# Revit family: A1-160-B
name_source: partatom
category: Structural Connections
revit_build: Autodesk Revit 2015 (Build: 20140606_1530(x64)
units: mm (PartAtom-declared; Revit-internal decimal feet)

## types (1)
- A1-160-B
    Default Elevation = 0 mm  [stored 0 ft]
    Density = 0.34 kg
    Description = Connector Other
    EPD = https://www.strongtie.eu
    ETA / DoP = https://www.strongtie.eu
    Manufacturer = Simpson Strong-Tie
    Model = A1-160-B
    Model Disclaimer = Contact Simpson Strong-Tie Company  for more information
    Model ID = 0303598991321790858711374912692772503994
    Name = A1-160-B
    ObjectType = A1-160-B
    Product Material = Aluminium
    Product Type = Connector Other
    Reference = A1-160-B
    Technical datasheet = https://www.strongtie.eu
    URL = www.strongtie.eu
    UniClass Number = Pr_20_85_09_52
    UniClass Title = Metal timber member fixing brackets

note: [stored X ft] marks values corroborated as IEEE doubles in the binary element streams (Revit-internal decimal feet)

## geometry (parser evidence)
native form markers: Blend x24, Sweep x3
no freeform markers — native parametric forms only
